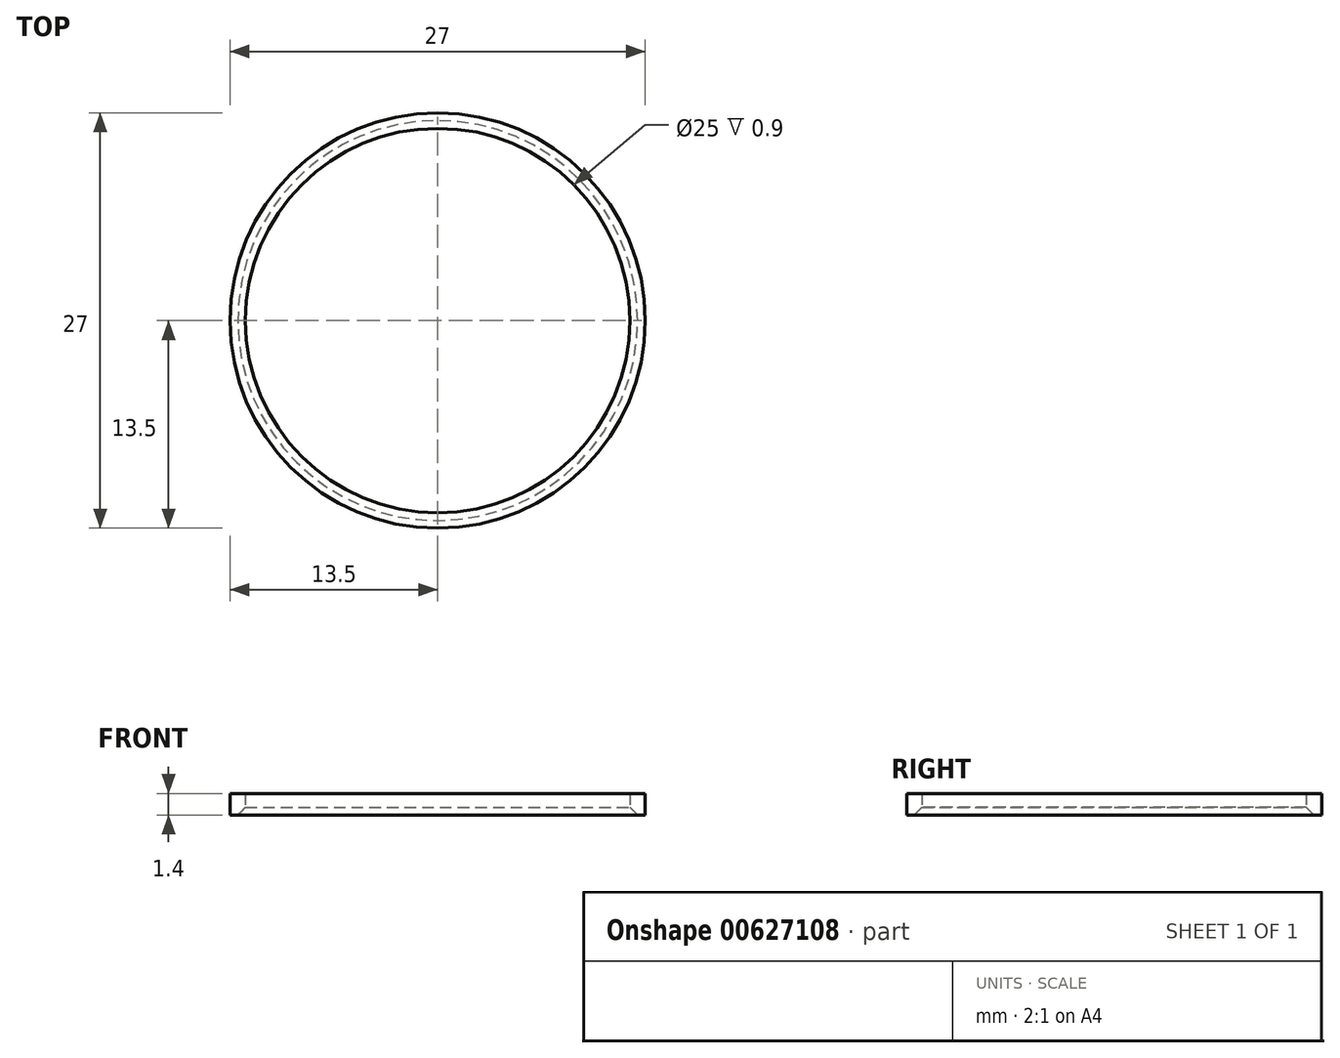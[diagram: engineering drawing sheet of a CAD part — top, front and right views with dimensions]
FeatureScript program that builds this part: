
annotation { "Feature Type Name" : "Feature", "Feature Type Description" : "" }
export const myFeature = defineFeature(function(context is Context, id is Id, definition is map)
    precondition{}
    {
        {
            var Q0;
            Q0=qCreatedBy(makeId("Front.planeOp"),FACE);
            var sketch = newSketch(context, id + "F0", { "sketchPlane" : qUnion([Q0])});
            skLineSegment(sketch, "E0", {"start": v(13.5, 0) * mm, "end": v(13.5, 1.4) * mm});
            skLineSegment(sketch, "E1", {"start": v(13.5, 1.4) * mm, "end": v(12.5, 1.4) * mm});
            skLineSegment(sketch, "E2", {"start": v(12.5, 1.4) * mm, "end": v(12.5, 0.5) * mm});
            skLineSegment(sketch, "E3", {"start": v(12.5, 0.5) * mm, "end": v(13, 0) * mm});
            skLineSegment(sketch, "E4", {"start": v(13, 0) * mm, "end": v(13.5, 0) * mm});
            skLineSegment(sketch, "E5", {"start": v(0, 0) * mm, "end": v(0, 4.26) * mm, "construction": true});
            skSolve(sketch);
        }
        {
            var Q0;
            Q0=makeQuery(id+"F0.imprint","IMPRINT",FACE,{"disambiguationData":[TD([[makeQuery(id+"F0.imprint","IMPRINT",EDGE,{"derivedFrom":sQuery(id+"F0.wireOp",EDGE,"E0")}),1.0]])]});
            var Q1;
            Q1=sQuery(id+"F0.wireOp",EDGE,"E5");
            revolve(context, id + "F1", {"entities" : qUnion([Q0]), "axis" : qUnion([Q1]), "revolveType" : RevolveType.FULL});
        }
    });
